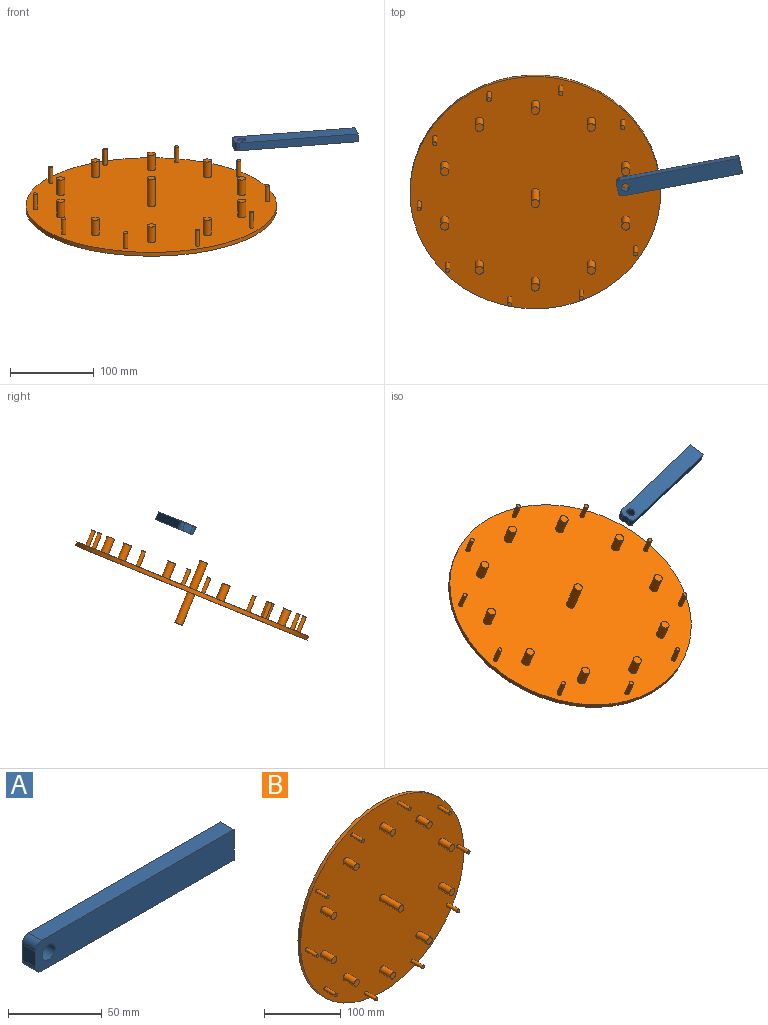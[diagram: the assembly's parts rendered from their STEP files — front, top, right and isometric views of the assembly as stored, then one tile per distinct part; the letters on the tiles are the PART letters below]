
ASSEMBLY  parts=2 mates=1
PART A: 9 faces, bbox 150x10x20 mm
  f0: plane 145x10mm, normal (0,0,1), area 1450mm2, adj f1,f5,f7,f8
  f1: cylinder r=5mm len=10mm, axis (0,1,0), area 78.5mm2, adj f0,f2,f7,f8
  f2: plane 10x10mm, normal (-1,0,0), area 100mm2, adj f1,f3,f7,f8
  f3: cylinder r=5mm len=10mm, axis (0,1,0), area 78.5mm2, adj f2,f4,f7,f8
  f4: plane 145x10mm, normal (0,0,-1), area 1450mm2, adj f3,f5,f7,f8
  f5: plane 20x10mm, normal (1,0,0), area 200mm2, adj f0,f4,f7,f8
  f6: cylinder r=5mm len=10mm, axis (0,1,0), area 314.2mm2, adj f7,f8
  f7: plane 150x20mm, normal (0,-1,0), area 2910.7mm2, adj f0,f1,f2,f3,f4,f5,f6
  f8: plane 150x20mm, normal (0,1,0), area 2910.7mm2, adj f0,f1,f2,f3,f4,f5,f6
PART B: 47 faces, bbox 300x80x300 mm
  f0: cylinder r=150mm len=300mm, axis (0,1,0), area 4712.4mm2, adj f1,f2
  f1: plane 300x300mm, normal (0,-1,0), area 69625.5mm2, adj f0,f3,f5,f7,f9,f11,f13,f15
  f2: plane 300x300mm, normal (0,1,0), area 70607.3mm2, adj f0,f44
  f3: cylinder r=5mm len=20mm, axis (0,1,0), area 628.3mm2, adj f1,f4
  f4: plane 10x10mm, normal (0,-1,0), area 78.5mm2, adj f3
  f5: cylinder r=5mm len=20mm, axis (0,1,0), area 628.3mm2, adj f1,f6
  f6: plane 10x10mm, normal (0,-1,0), area 78.5mm2, adj f5
  f7: cylinder r=5mm len=20mm, axis (0,1,0), area 628.3mm2, adj f1,f8
  f8: plane 10x10mm, normal (0,-1,0), area 78.5mm2, adj f7
  f9: cylinder r=5mm len=20mm, axis (0,1,0), area 628.3mm2, adj f1,f10
  f10: plane 10x10mm, normal (0,-1,0), area 78.5mm2, adj f9
  f11: cylinder r=5mm len=20mm, axis (0,1,0), area 628.3mm2, adj f1,f12
  f12: plane 10x10mm, normal (0,-1,0), area 78.5mm2, adj f11
  f13: cylinder r=5mm len=20mm, axis (0,1,0), area 628.3mm2, adj f1,f14
  f14: plane 10x10mm, normal (0,-1,0), area 78.5mm2, adj f13
  f15: cylinder r=5mm len=20mm, axis (0,1,0), area 628.3mm2, adj f1,f16
  f16: plane 10x10mm, normal (0,-1,0), area 78.5mm2, adj f15
  f17: cylinder r=5mm len=20mm, axis (0,1,0), area 628.3mm2, adj f1,f18
  f18: plane 10x10mm, normal (0,-1,0), area 78.5mm2, adj f17
  f19: cylinder r=5mm len=20mm, axis (0,1,0), area 628.3mm2, adj f1,f20
  f20: plane 10x10mm, normal (0,-1,0), area 78.5mm2, adj f19
  f21: cylinder r=5mm len=20mm, axis (0,1,0), area 628.3mm2, adj f1,f22
  f22: plane 10x10mm, normal (0,-1,0), area 78.5mm2, adj f21
  f23: cylinder r=2.5mm len=20mm, axis (0,1,0), area 314.2mm2, adj f1,f24
  f24: plane 5x5mm, normal (0,-1,0), area 19.6mm2, adj f23
  f25: cylinder r=2.5mm len=20mm, axis (0,1,0), area 314.2mm2, adj f1,f26
  f26: plane 5x5mm, normal (0,-1,0), area 19.6mm2, adj f25
  f27: cylinder r=2.5mm len=20mm, axis (0,1,0), area 314.2mm2, adj f1,f28
  f28: plane 5x5mm, normal (0,-1,0), area 19.6mm2, adj f27
  f29: cylinder r=2.5mm len=20mm, axis (0,1,0), area 314.2mm2, adj f1,f30
  f30: plane 5x5mm, normal (0,-1,0), area 19.6mm2, adj f29
  f31: cylinder r=2.5mm len=20mm, axis (0,1,0), area 314.2mm2, adj f1,f32
  f32: plane 5x5mm, normal (0,-1,0), area 19.6mm2, adj f31
  f33: cylinder r=2.5mm len=20mm, axis (0,1,0), area 314.2mm2, adj f1,f34
  f34: plane 5x5mm, normal (0,-1,0), area 19.6mm2, adj f33
  f35: cylinder r=2.5mm len=20mm, axis (0,1,0), area 314.2mm2, adj f1,f36
  f36: plane 5x5mm, normal (0,-1,0), area 19.6mm2, adj f35
  f37: cylinder r=2.5mm len=20mm, axis (0,1,0), area 314.2mm2, adj f1,f38
  f38: plane 5x5mm, normal (0,-1,0), area 19.6mm2, adj f37
  f39: cylinder r=2.5mm len=20mm, axis (0,1,0), area 314.2mm2, adj f1,f40
  f40: plane 5x5mm, normal (0,-1,0), area 19.6mm2, adj f39
  f41: cylinder r=2.5mm len=20mm, axis (0,1,0), area 314.2mm2, adj f1,f42
  f42: plane 5x5mm, normal (0,-1,0), area 19.6mm2, adj f41
  f43: plane 10x10mm, normal (0,1,0), area 78.5mm2, adj f44
  f44: cylinder r=5mm len=40mm, axis (0,1,0), area 1256.6mm2, adj f2,f43
  f45: cylinder r=5mm len=35mm, axis (0,1,0), area 1099.6mm2, adj f1,f46
  f46: plane 10x10mm, normal (0,-1,0), area 78.5mm2, adj f45
PLACE A rot(axis=(-0.98,-0.15,0.1),68.7deg) t=(107.33,-17.35,23.2)mm
PLACE B rot(axis=(-1,0,0),67.8deg) t=(6.9,-14.41,-46.05)mm
MATE cylindrical A.f6 <-> B.f7  axis (0,0.38,-0.93) through (115.31,-10.18,36.92)mm
